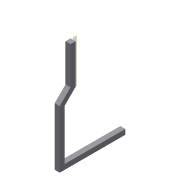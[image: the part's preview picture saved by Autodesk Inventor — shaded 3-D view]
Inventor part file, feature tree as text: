
AUTODESK INVENTOR PART (.ipt)
format: ipt  version: 2019 (Build 230136000, 136)  size: 105,984 bytes
history: native  units: mm
features: other x3, extrude x2, sketch x2, plane x1, chamfer x1, reference x1, projected_geometry x1
ambient origin geometry x8: Origin, YZ Plane, XZ Plane, XY Plane, X Axis, Y Axis, Z Axis, Center Point
bodies: Volumenkörper1 (feature_tree)
feature tree (11):
  plane  "Arbeitsebene1"
  extrude  "Extrusion1"  Depth=5.0mm
  extrude  "Extrusion2"  Depth=5.0mm
  chamfer  "Fase1"  Distance=5.0mm
  sketch  "Skizze1"  dims[d0=45.0deg d1=5.0mm]
  reference  "Referenz1"
  sketch  "Skizze2"  dims[d2=5.0mm d3=5.0mm d4=5.0mm d5=60.0mm d6=50.0mm d7=5.0mm d8=0.0mm d9=1.8mm d10=1.8mm d11=5.0mm d12=0.0mm d13=5.0mm d14=2.0mm d15=45.0deg]
  projected_geometry  "Projizierte Kontur1"
  other  "<userpath>\Documents\Inventor\HITscope\Full_HITscope_v0.iam"
  other  "Full_HITscope_v0.iam"
  other  "05_Omniscope_base_v1:1"
